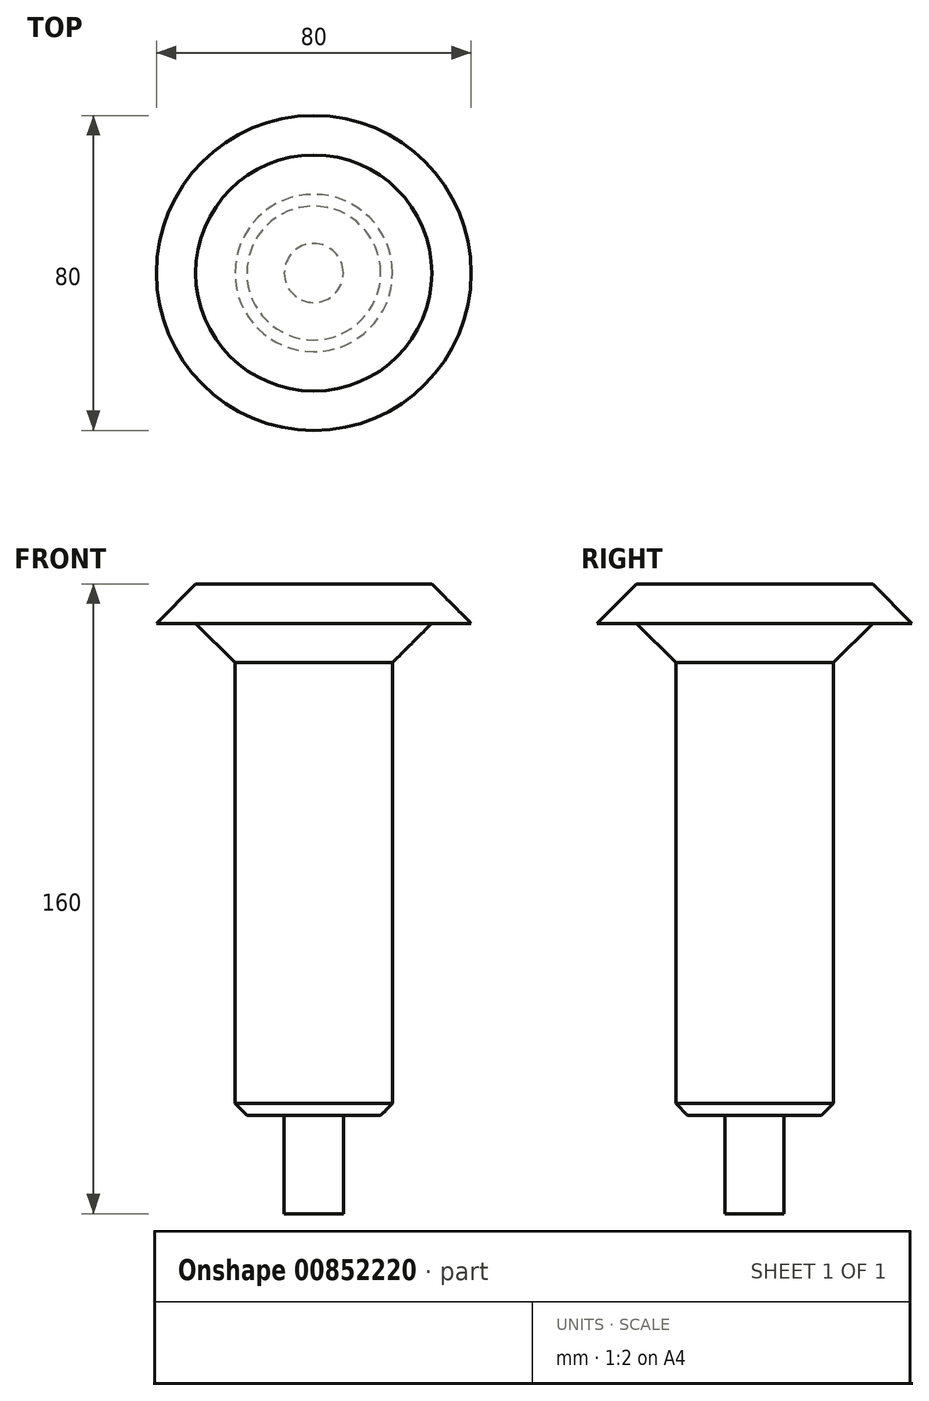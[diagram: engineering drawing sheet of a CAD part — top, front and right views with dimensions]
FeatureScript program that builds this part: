
annotation { "Feature Type Name" : "Feature", "Feature Type Description" : "" }
export const myFeature = defineFeature(function(context is Context, id is Id, definition is map)
    precondition{}
    {
        {
            var Q0;
            Q0=qCreatedBy(makeId("Front.planeOp"),FACE);
            var sketch = newSketch(context, id + "F0", { "sketchPlane" : qUnion([Q0])});
            skLineSegment(sketch, "E0", {"start": v(0, 0) * mm, "end": v(-7.5, 0) * mm});
            skLineSegment(sketch, "E1", {"start": v(-7.5, 0) * mm, "end": v(-7.5, 25) * mm});
            skLineSegment(sketch, "E2", {"start": v(-7.5, 25) * mm, "end": v(-20, 25) * mm});
            skLineSegment(sketch, "E3", {"start": v(-20, 25) * mm, "end": v(-20, 140) * mm});
            skLineSegment(sketch, "E4", {"start": v(-20, 140) * mm, "end": v(-30, 150) * mm});
            skLineSegment(sketch, "E5", {"start": v(-30, 150) * mm, "end": v(-40, 150) * mm});
            skLineSegment(sketch, "E6", {"start": v(-40, 150) * mm, "end": v(-30, 160) * mm});
            skLineSegment(sketch, "E7", {"start": v(-30, 160) * mm, "end": v(0, 160) * mm});
            skLineSegment(sketch, "E8", {"start": v(0, 160) * mm, "end": v(0, 0) * mm});
            skSolve(sketch);
        }
        {
            var Q0;
            Q0 = qSketchRegion(id + "F0", true);
            var Q1;
            Q1=sQuery(id+"F0.wireOp",EDGE,"E8");
            revolve(context, id + "F1", {"surfaceOperationType" : NewSurfaceOperationType.NEW, "entities" : qUnion([Q0]), "axis" : qUnion([Q1]), "revolveType" : RevolveType.FULL});
        }
        {
            var Q0;
            Q0=makeQuery(id+"F1.opRevolve","SWEPT_EDGE",EDGE,{"disambiguationData":[OSD([sQuery(id+"F0.wireOp",EDGE,"E2"),sQuery(id+"F0.wireOp",EDGE,"E3")])]});
            chamfer(context, id + "F2", {"entities" : qUnion([Q0]), "width" : 3 * mm, "tangentPropagation" : true});
        }
    });
